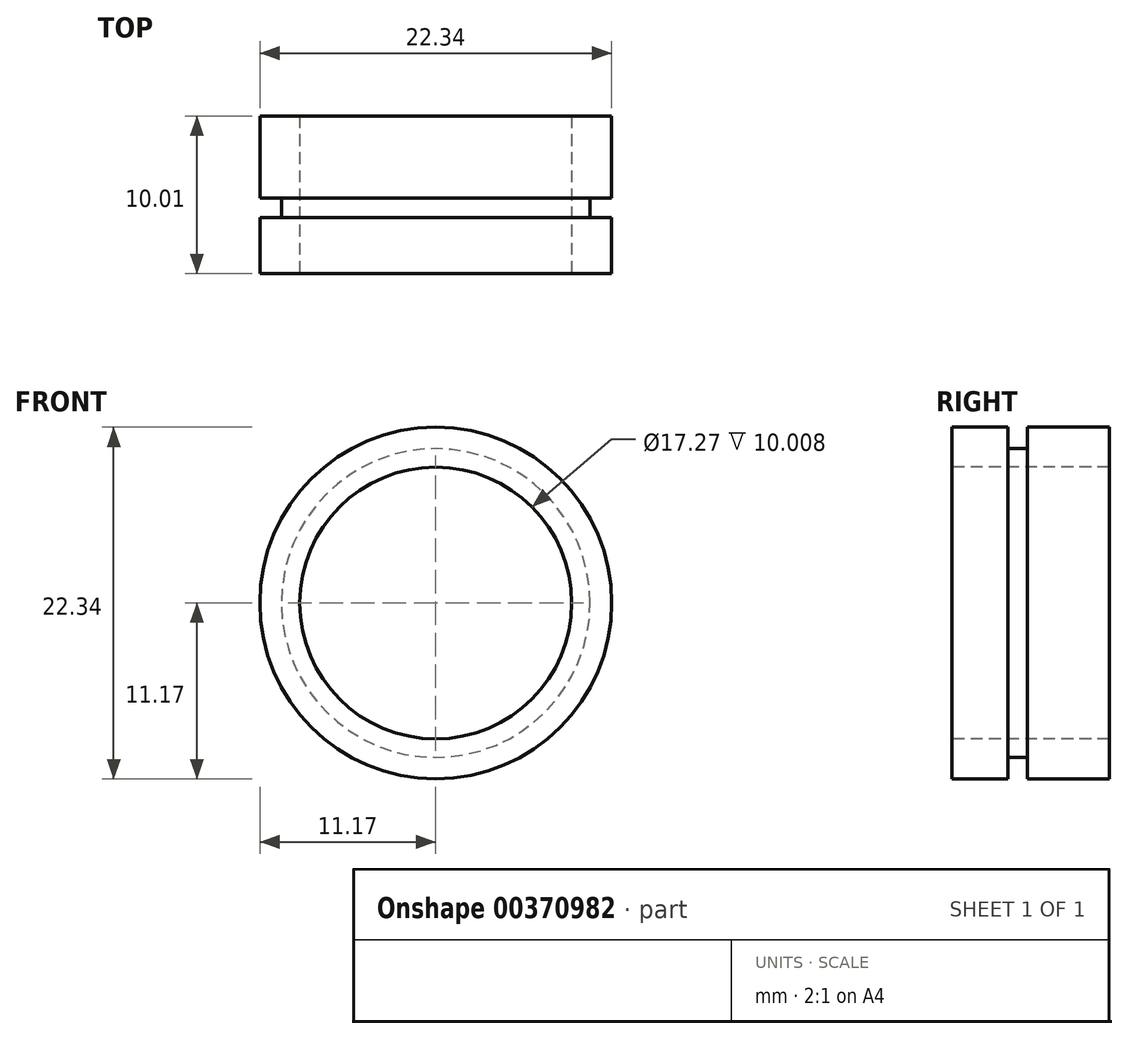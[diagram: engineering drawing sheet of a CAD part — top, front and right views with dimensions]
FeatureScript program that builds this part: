
annotation { "Feature Type Name" : "Feature", "Feature Type Description" : "" }
export const myFeature = defineFeature(function(context is Context, id is Id, definition is map)
    precondition{}
    {
        {
            var Q0;
            Q0=qCreatedBy(makeId("Right.planeOp"),FACE);
            var sketch = newSketch(context, id + "F0", { "sketchPlane" : qUnion([Q0])});
            skLineSegment(sketch, "E0.bottom", {"start": v(0, 8.63) * mm, "end": v(3.56, 8.63) * mm});
            skLineSegment(sketch, "E0.top", {"start": v(0, 11.17) * mm, "end": v(3.56, 11.17) * mm});
            skLineSegment(sketch, "E0.left", {"start": v(0, 8.63) * mm, "end": v(0, 11.17) * mm});
            skLineSegment(sketch, "E0.right", {"start": v(3.56, 8.63) * mm, "end": v(3.56, 11.17) * mm});
            skLineSegment(sketch, "E1.bottom", {"start": v(3.56, 8.63) * mm, "end": v(4.8, 8.63) * mm});
            skLineSegment(sketch, "E1.top", {"start": v(3.56, 9.8) * mm, "end": v(4.8, 9.8) * mm});
            skLineSegment(sketch, "E1.left", {"start": v(3.56, 8.63) * mm, "end": v(3.56, 9.8) * mm});
            skLineSegment(sketch, "E1.right", {"start": v(4.8, 8.63) * mm, "end": v(4.8, 9.8) * mm});
            skLineSegment(sketch, "E2.bottom", {"start": v(4.8, 8.63) * mm, "end": v(10, 8.63) * mm});
            skLineSegment(sketch, "E2.top", {"start": v(4.8, 11.17) * mm, "end": v(10, 11.17) * mm});
            skLineSegment(sketch, "E2.left", {"start": v(4.8, 8.63) * mm, "end": v(4.8, 11.17) * mm});
            skLineSegment(sketch, "E2.right", {"start": v(10, 8.63) * mm, "end": v(10, 11.17) * mm});
            skLineSegment(sketch, "E3", {"start": v(0, 0) * mm, "end": v(10.53, 0) * mm, "construction": true});
            skLineSegment(sketch, "E4.MirrorCS", {"start": v(3.56, -8.63) * mm, "end": v(4.8, -8.63) * mm});
            skLineSegment(sketch, "E5.MirrorCS", {"start": v(3.56, -9.8) * mm, "end": v(4.8, -9.8) * mm});
            skLineSegment(sketch, "E6.MirrorCS", {"start": v(4.8, -8.63) * mm, "end": v(4.8, -9.8) * mm});
            skLineSegment(sketch, "E7.MirrorCS", {"start": v(3.56, -8.63) * mm, "end": v(3.56, -11.17) * mm});
            skLineSegment(sketch, "E8.MirrorCS", {"start": v(3.56, -8.63) * mm, "end": v(3.56, -9.8) * mm});
            skLineSegment(sketch, "E9.MirrorCS", {"start": v(4.8, -8.63) * mm, "end": v(4.8, -11.17) * mm});
            skLineSegment(sketch, "E10.MirrorCS", {"start": v(10, -8.63) * mm, "end": v(10, -11.17) * mm});
            skLineSegment(sketch, "E11.MirrorCS", {"start": v(4.8, -8.63) * mm, "end": v(10, -8.63) * mm});
            skLineSegment(sketch, "E12.MirrorCS", {"start": v(0, -8.63) * mm, "end": v(3.56, -8.63) * mm});
            skLineSegment(sketch, "E13.MirrorCS", {"start": v(0, -11.17) * mm, "end": v(3.56, -11.17) * mm});
            skLineSegment(sketch, "E14.MirrorCS", {"start": v(4.8, -11.17) * mm, "end": v(10, -11.17) * mm});
            skLineSegment(sketch, "E15.MirrorCS", {"start": v(0, -8.63) * mm, "end": v(0, -11.17) * mm});
            skSolve(sketch);
        }
        {
            var Q0;
            Q0=makeQuery(id+"F0.imprint","IMPRINT",FACE,{"disambiguationData":[TD([[makeQuery(id+"F0.imprint","IMPRINT",EDGE,{"derivedFrom":sQuery(id+"F0.wireOp",EDGE,"E0.bottom")}),1.0]])]});
            var Q1;
            {var subQ0=sQuery(id+"F0.wireOp",EDGE,"E1.bottom");Q1=makeQuery(id+"F0.imprint","IMPRINT",FACE,{"disambiguationData":[TD([[makeQuery(id+"F0.imprint","IMPRINT",EDGE,{"derivedFrom":subQ0}),1.0]])]});}
            var Q2;
            {var subQ3=sQuery(id+"F0.wireOp",EDGE,"E2.bottom");Q2=makeQuery(id+"F0.imprint","IMPRINT",FACE,{"disambiguationData":[TD([[makeQuery(id+"F0.imprint","IMPRINT",EDGE,{"derivedFrom":subQ3}),1.0]])]});}
            var Q3;
            Q3=sQuery(id+"F0.wireOp",EDGE,"E3");
            revolve(context, id + "F1", {"entities" : qUnion([Q0, Q1, Q2]), "axis" : qUnion([Q3]), "revolveType" : RevolveType.FULL});
        }
    });
